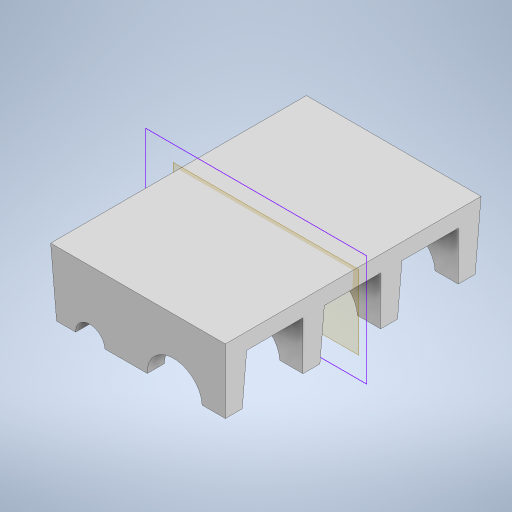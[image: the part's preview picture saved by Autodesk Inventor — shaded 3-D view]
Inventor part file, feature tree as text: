
AUTODESK INVENTOR PART (.ipt)
format: ipt  version: 2023 (Build 270158000, 158)  size: 294,400 bytes
history: native  units: in
note: dims shown in document units (in); Inventor stores cm internally (conversion verified against a paired STEP export)
features: extrude x2, sketch x2, plane x1, draft x1
ambient origin geometry x8: Origin, YZ Plane, XZ Plane, XY Plane, X Axis, Y Axis, Z Axis, Center Point
bodies: Solid1 (feature_tree)
feature tree (6):
  extrude  "Extrusion1"  Depth=5.0in
  extrude  "Extrusion2"  Depth=0.5in
  plane  "Work Plane1"
  sketch  "Sketch5"  dims[d3=7.4in d4=0.0in d15=1.4in d16=3.7in d17=6.0in d18=0.5in d20=2.528in d21=7.4in d22=0.0in d25=1.5in d26=0.866in d31=1.2546in d32=0.5669in d33=2.0in d34=1.5in d35=0.0172in d27=0.5in d28=0.0344in d29=0.0in d30=0.0in d36=0.5in d37=0.0344in d38=0.5in d39=0.0344in]
  draft  "FaceDraft1"
  sketch  "Sketch1"  dims[d0=5.0in d2=1.625in]
